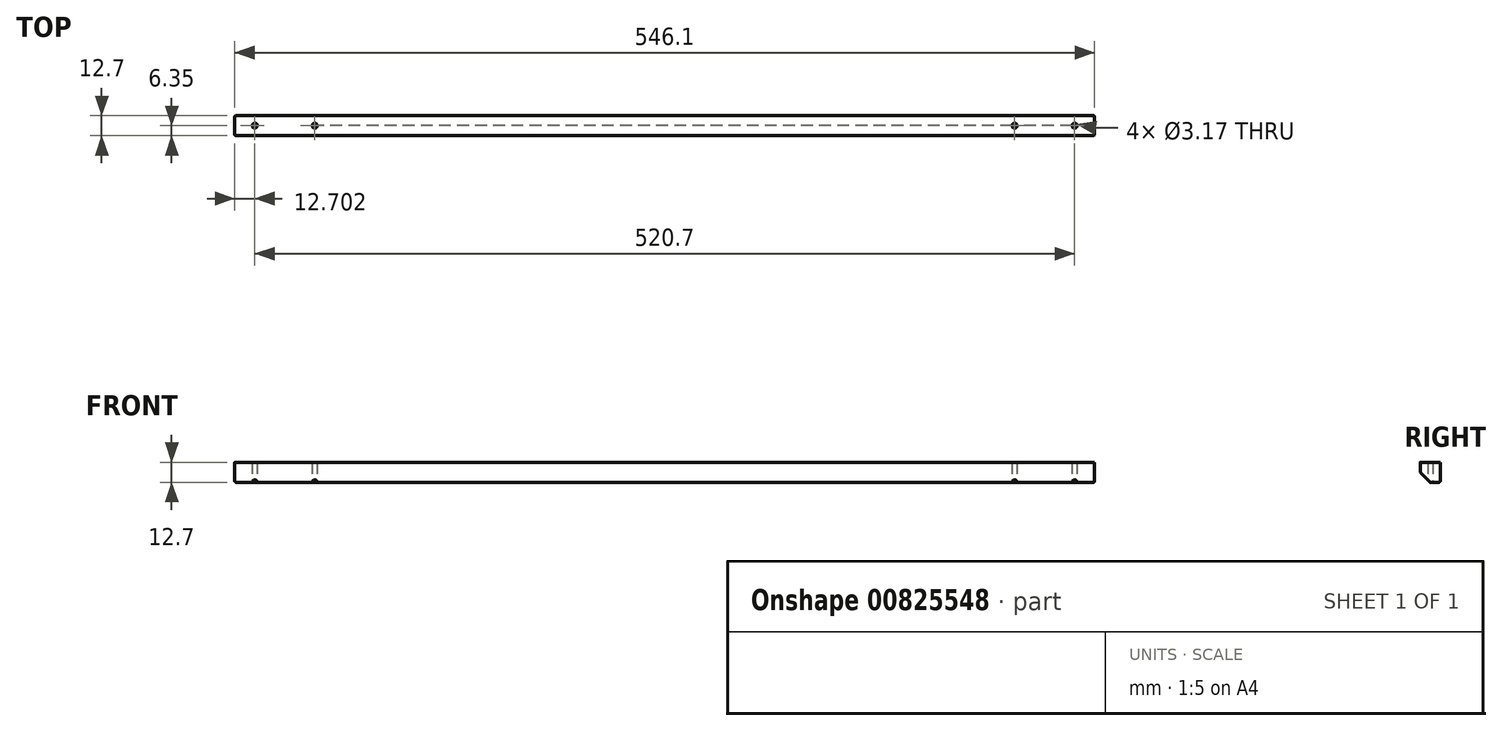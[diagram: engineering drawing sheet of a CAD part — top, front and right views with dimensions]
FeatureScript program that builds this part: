
annotation { "Feature Type Name" : "Feature", "Feature Type Description" : "" }
export const myFeature = defineFeature(function(context is Context, id is Id, definition is map)
    precondition{}
    {
        {
            var Q0;
            Q0=qCreatedBy(makeId("Top.planeOp"),FACE);
            var sketch = newSketch(context, id + "F0", { "sketchPlane" : qUnion([Q0])});
            skLineSegment(sketch, "E0.bottom", {"start": v(-268.66, -6.35) * mm, "end": v(277.44, -6.35) * mm});
            skLineSegment(sketch, "E0.top", {"start": v(-268.66, 6.35) * mm, "end": v(277.44, 6.35) * mm});
            skLineSegment(sketch, "E0.left", {"start": v(-268.66, -6.35) * mm, "end": v(-268.66, 6.35) * mm});
            skLineSegment(sketch, "E0.right", {"start": v(277.44, -6.35) * mm, "end": v(277.44, 6.35) * mm});
            skPoint(sketch, "E0.middle", {"position": v(4.4, 0) * mm});
            skCircle(sketch, "E1", {"center": v(-255.96, 0) * mm, "radius": 1.59 * mm});
            skCircle(sketch, "E2", {"center": v(-217.86, 0) * mm, "radius": 1.59 * mm});
            skCircle(sketch, "E3", {"center": v(226.64, 0) * mm, "radius": 1.59 * mm});
            skCircle(sketch, "E4", {"center": v(264.74, 0) * mm, "radius": 1.59 * mm});
            skSolve(sketch);
        }
        {
            var Q0;
            Q0=makeQuery(id+"F0.imprint","IMPRINT",FACE,{"disambiguationData":[TD([[makeQuery(id+"F0.imprint","IMPRINT",EDGE,{"derivedFrom":sQuery(id+"F0.wireOp",EDGE,"E0.bottom")}),1.0]])]});
            extrude(context, id + "F1", {"entities" : qUnion([Q0]), "endBound" : BoundingType.SYMMETRIC, "depth" : 12.7 * mm, "offsetDistance" : 25.4 * mm});
        }
        {
            var Q0;
            Q0=makeQuery(id+"F1.opExtrude","CAP_EDGE",EDGE,{"disambiguationData":[OSD([sQuery(id+"F0.wireOp",EDGE,"E0.bottom")])],"isStart":true});
            chamfer(context, id + "F2", {"entities" : qUnion([Q0]), "width" : 6.35 * mm, "tangentPropagation" : true});
        }
        {
            var Q0;
            Q0=makeQuery(id+"F2.opChamfer","BLEND_EDGE",EDGE,{"blendedFrom":[makeQuery(id+"F1.opExtrude","CAP_EDGE",EDGE,{"disambiguationData":[OSD([sQuery(id+"F0.wireOp",EDGE,"E0.bottom")])],"isStart":true}),makeQuery(id+"F1.opExtrude","SWEPT_FACE",FACE,{"disambiguationData":[OSD([sQuery(id+"F0.wireOp",EDGE,"E0.right")])]})],"blendedInto":[makeQuery(id+"F1.opExtrude","SWEPT_FACE",FACE,{"disambiguationData":[OSD([sQuery(id+"F0.wireOp",EDGE,"E0.right")])]})]});
            var Q1;
            Q1=makeQuery(id+"F1.opExtrude","SWEPT_EDGE",EDGE,{"disambiguationData":[OSD([sQuery(id+"F0.wireOp",EDGE,"E0.bottom"),sQuery(id+"F0.wireOp",EDGE,"E0.right")])]});
            var Q2;
            Q2=makeQuery(id+"F1.opExtrude","CAP_EDGE",EDGE,{"disambiguationData":[OSD([sQuery(id+"F0.wireOp",EDGE,"E0.right")])],"isStart":true});
            var Q3;
            Q3=makeQuery(id+"F1.opExtrude","SWEPT_EDGE",EDGE,{"disambiguationData":[OSD([sQuery(id+"F0.wireOp",EDGE,"E0.top"),sQuery(id+"F0.wireOp",EDGE,"E0.right")])]});
            var Q4;
            Q4=makeQuery(id+"F2.opChamfer","BLEND_EDGE",EDGE,{"blendedFrom":[makeQuery(id+"F1.opExtrude","CAP_EDGE",EDGE,{"disambiguationData":[OSD([sQuery(id+"F0.wireOp",EDGE,"E0.bottom")])],"isStart":true}),makeQuery(id+"F1.opExtrude","SWEPT_FACE",FACE,{"disambiguationData":[OSD([sQuery(id+"F0.wireOp",EDGE,"E0.left")])]})],"blendedInto":[makeQuery(id+"F1.opExtrude","SWEPT_FACE",FACE,{"disambiguationData":[OSD([sQuery(id+"F0.wireOp",EDGE,"E0.left")])]})]});
            var Q5;
            Q5=makeQuery(id+"F1.opExtrude","SWEPT_EDGE",EDGE,{"disambiguationData":[OSD([sQuery(id+"F0.wireOp",EDGE,"E0.bottom"),sQuery(id+"F0.wireOp",EDGE,"E0.left")])]});
            var Q6;
            Q6=makeQuery(id+"F1.opExtrude","CAP_EDGE",EDGE,{"disambiguationData":[OSD([sQuery(id+"F0.wireOp",EDGE,"E0.left")])],"isStart":true});
            var Q7;
            Q7=makeQuery(id+"F1.opExtrude","SWEPT_EDGE",EDGE,{"disambiguationData":[OSD([sQuery(id+"F0.wireOp",EDGE,"E0.top"),sQuery(id+"F0.wireOp",EDGE,"E0.left")])]});
            var Q8;
            {var subQ0=sQuery(id+"F0.wireOp",EDGE,"E0.bottom");Q8=makeQuery(id+"F2.opChamfer","BLEND_EDGE",EDGE,{"blendedFrom":[makeQuery(id+"F1.opExtrude","CAP_EDGE",EDGE,{"disambiguationData":[OSD([subQ0])],"isStart":true}),makeQuery(id+"F1.opExtrude","SWEPT_FACE",FACE,{"disambiguationData":[OSD([subQ0])]})],"blendedInto":[makeQuery(id+"F1.opExtrude","SWEPT_FACE",FACE,{"disambiguationData":[OSD([subQ0])]})]});}
            var Q9;
            {var subQ0=sQuery(id+"F0.wireOp",EDGE,"E0.bottom");Q9=makeQuery(id+"F2.opChamfer","BLEND_EDGE",EDGE,{"disambiguationData":[OD(2.0)],"blendedFrom":[makeQuery(id+"F1.opExtrude","CAP_EDGE",EDGE,{"disambiguationData":[OSD([subQ0])],"isStart":true}),makeQuery(id+"F1.opExtrude","CAP_FACE",FACE,{"disambiguationData":[OSD([subQ0,sQuery(id+"F0.wireOp",EDGE,"E0.top"),sQuery(id+"F0.wireOp",EDGE,"E0.left"),sQuery(id+"F0.wireOp",EDGE,"E0.right"),sQuery(id+"F0.wireOp",EDGE,"tNNlBU02-CvaY-YdCE-Ffe3-kxiK19WcpfAm"),sQuery(id+"F0.wireOp",EDGE,"JQ2wRuE7-nnvd-dPdz-saey-PttIh5TRXWeP")])],"isStart":true})],"blendedInto":[makeQuery(id+"F1.opExtrude","CAP_FACE",FACE,{"disambiguationData":[OSD([subQ0,sQuery(id+"F0.wireOp",EDGE,"E0.top"),sQuery(id+"F0.wireOp",EDGE,"E0.left"),sQuery(id+"F0.wireOp",EDGE,"E0.right"),sQuery(id+"F0.wireOp",EDGE,"tNNlBU02-CvaY-YdCE-Ffe3-kxiK19WcpfAm"),sQuery(id+"F0.wireOp",EDGE,"JQ2wRuE7-nnvd-dPdz-saey-PttIh5TRXWeP")])],"isStart":true})]});}
            var Q10;
            {var subQ0=sQuery(id+"F0.wireOp",EDGE,"E0.bottom");Q10=makeQuery(id+"F2.opChamfer","BLEND_EDGE",EDGE,{"disambiguationData":[OD(0.0)],"blendedFrom":[makeQuery(id+"F1.opExtrude","CAP_EDGE",EDGE,{"disambiguationData":[OSD([subQ0])],"isStart":true}),makeQuery(id+"F1.opExtrude","CAP_FACE",FACE,{"disambiguationData":[OSD([subQ0,sQuery(id+"F0.wireOp",EDGE,"E0.top"),sQuery(id+"F0.wireOp",EDGE,"E0.left"),sQuery(id+"F0.wireOp",EDGE,"E0.right"),sQuery(id+"F0.wireOp",EDGE,"tNNlBU02-CvaY-YdCE-Ffe3-kxiK19WcpfAm"),sQuery(id+"F0.wireOp",EDGE,"JQ2wRuE7-nnvd-dPdz-saey-PttIh5TRXWeP")])],"isStart":true})],"blendedInto":[makeQuery(id+"F1.opExtrude","CAP_FACE",FACE,{"disambiguationData":[OSD([subQ0,sQuery(id+"F0.wireOp",EDGE,"E0.top"),sQuery(id+"F0.wireOp",EDGE,"E0.left"),sQuery(id+"F0.wireOp",EDGE,"E0.right"),sQuery(id+"F0.wireOp",EDGE,"tNNlBU02-CvaY-YdCE-Ffe3-kxiK19WcpfAm"),sQuery(id+"F0.wireOp",EDGE,"JQ2wRuE7-nnvd-dPdz-saey-PttIh5TRXWeP")])],"isStart":true})]});}
            var Q11;
            {var subQ0=sQuery(id+"F0.wireOp",EDGE,"E0.bottom");Q11=makeQuery(id+"F2.opChamfer","BLEND_EDGE",EDGE,{"disambiguationData":[OD(1.0)],"blendedFrom":[makeQuery(id+"F1.opExtrude","CAP_EDGE",EDGE,{"disambiguationData":[OSD([subQ0])],"isStart":true}),makeQuery(id+"F1.opExtrude","CAP_FACE",FACE,{"disambiguationData":[OSD([subQ0,sQuery(id+"F0.wireOp",EDGE,"E0.top"),sQuery(id+"F0.wireOp",EDGE,"E0.left"),sQuery(id+"F0.wireOp",EDGE,"E0.right"),sQuery(id+"F0.wireOp",EDGE,"tNNlBU02-CvaY-YdCE-Ffe3-kxiK19WcpfAm"),sQuery(id+"F0.wireOp",EDGE,"JQ2wRuE7-nnvd-dPdz-saey-PttIh5TRXWeP")])],"isStart":true})],"blendedInto":[makeQuery(id+"F1.opExtrude","CAP_FACE",FACE,{"disambiguationData":[OSD([subQ0,sQuery(id+"F0.wireOp",EDGE,"E0.top"),sQuery(id+"F0.wireOp",EDGE,"E0.left"),sQuery(id+"F0.wireOp",EDGE,"E0.right"),sQuery(id+"F0.wireOp",EDGE,"tNNlBU02-CvaY-YdCE-Ffe3-kxiK19WcpfAm"),sQuery(id+"F0.wireOp",EDGE,"JQ2wRuE7-nnvd-dPdz-saey-PttIh5TRXWeP")])],"isStart":true})]});}
            var Q12;
            Q12=makeQuery(id+"F1.opExtrude","CAP_EDGE",EDGE,{"disambiguationData":[OSD([sQuery(id+"F0.wireOp",EDGE,"E0.top")])],"isStart":true});
            fillet(context, id + "F3", {"entities" : qUnion([Q0, Q1, Q2, Q3, Q4, Q5, Q6, Q7, Q8, Q9, Q10, Q11, Q12]), "radius" : 0.8 * mm, "tangentPropagation" : true, "allowEdgeOverflow" : false});
        }
    });
